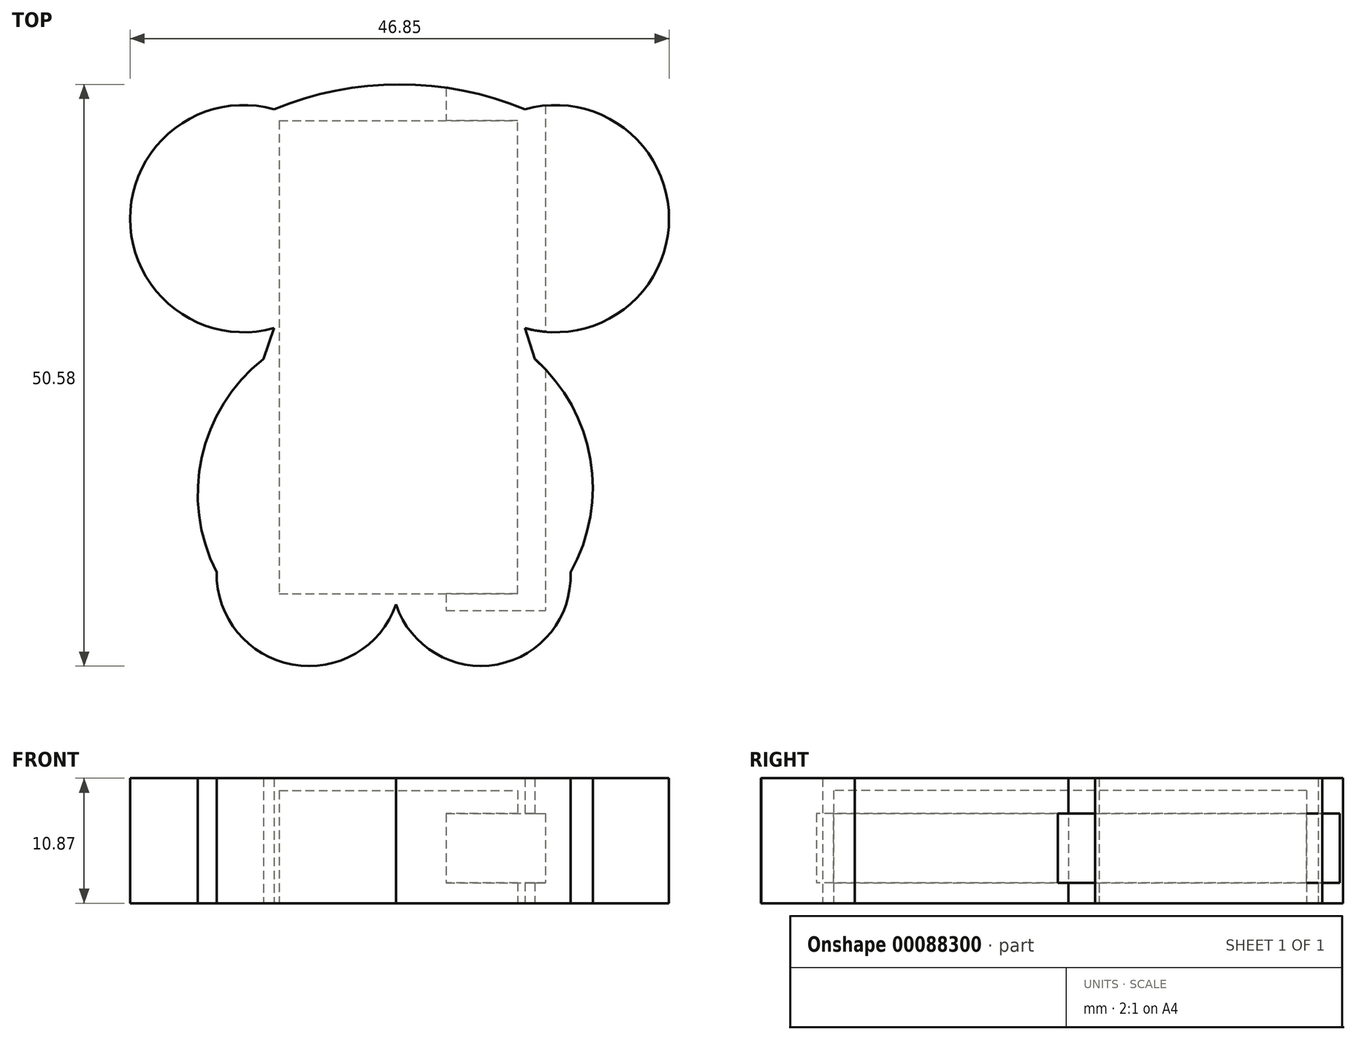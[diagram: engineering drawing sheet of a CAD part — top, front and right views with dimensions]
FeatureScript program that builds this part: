
annotation { "Feature Type Name" : "Feature", "Feature Type Description" : "" }
export const myFeature = defineFeature(function(context is Context, id is Id, definition is map)
    precondition{}
    {
        {
            var Q0;
            Q0=qCreatedBy(makeId("Top.planeOp"),FACE);
            var sketch = newSketch(context, id + "F0", { "sketchPlane" : qUnion([Q0])});
            skArc(sketch, "E0", {"start": v(-19.61, 43.61) * mm, "mid": v(-30.52, 45.76) * mm, "end": v(-41.42, 43.61) * mm});
            skArc(sketch, "E1", {"start": v(-19.61, 24.57) * mm, "mid": v(-7.1, 34.1) * mm, "end": v(-19.61, 43.61) * mm});
            skArc(sketch, "E2", {"start": v(-41.42, 43.61) * mm, "mid": v(-53.94, 34.1) * mm, "end": v(-41.42, 24.57) * mm});
            skLineSegment(sketch, "E3", {"start": v(-41.42, 24.57) * mm, "end": v(-42.36, 21.89) * mm});
            skLineSegment(sketch, "E4", {"start": v(-19.61, 24.57) * mm, "end": v(-18.76, 21.89) * mm});
            skArc(sketch, "E5", {"start": v(-42.36, 21.89) * mm, "mid": v(-47.71, 13.34) * mm, "end": v(-46.42, 3.33) * mm});
            skArc(sketch, "E6", {"start": v(-15.66, 3.33) * mm, "mid": v(-13.93, 13.16) * mm, "end": v(-18.76, 21.89) * mm});
            skArc(sketch, "E7", {"start": v(-30.75, 5.63) * mm, "mid": v(-24.6, -4.72) * mm, "end": v(-15.66, 3.33) * mm});
            skArc(sketch, "E8", {"start": v(-46.42, 3.33) * mm, "mid": v(-37.23, -4.74) * mm, "end": v(-30.75, 5.63) * mm});
            skSolve(sketch);
        }
        {
            var Q0;
            Q0 = qSketchRegion(id + "F0", true);
            extrude(context, id + "F1", {"entities" : qUnion([Q0]), "depth" : 10.87 * mm});
        }
        {
            var Q0;
            Q0=qCreatedBy(makeId("Top.planeOp"),FACE);
            var sketch = newSketch(context, id + "F2", { "sketchPlane" : qUnion([Q0])});
            skLineSegment(sketch, "E9.bottom", {"start": v(-40.99, 42.6) * mm, "end": v(-20.25, 42.6) * mm});
            skLineSegment(sketch, "E9.top", {"start": v(-40.99, 1.47) * mm, "end": v(-20.25, 1.47) * mm});
            skLineSegment(sketch, "E9.left", {"start": v(-40.99, 42.6) * mm, "end": v(-40.99, 1.47) * mm});
            skLineSegment(sketch, "E9.right", {"start": v(-20.25, 42.6) * mm, "end": v(-20.25, 1.47) * mm});
            skSolve(sketch);
        }
        {
            var Q0;
            Q0 = qSketchRegion(id + "F2", true);
            extrude(context, id + "F3", {"entities" : qUnion([Q0]), "operationType" : NewBodyOperationType.REMOVE, "depth" : 9.79 * mm});
        }
        {
            var Q0;
            Q0=qCreatedBy(makeId("Front.planeOp"),FACE);
            var sketch = newSketch(context, id + "F4", { "sketchPlane" : qUnion([Q0])});
            skLineSegment(sketch, "E10.bottom", {"start": v(-26.46, 7.78) * mm, "end": v(-17.83, 7.78) * mm});
            skLineSegment(sketch, "E10.top", {"start": v(-26.46, 1.78) * mm, "end": v(-17.83, 1.78) * mm});
            skLineSegment(sketch, "E10.left", {"start": v(-26.46, 7.78) * mm, "end": v(-26.46, 1.78) * mm});
            skLineSegment(sketch, "E10.right", {"start": v(-17.83, 7.78) * mm, "end": v(-17.83, 1.78) * mm});
            skSolve(sketch);
        }
        {
            var Q0;
            Q0 = qSketchRegion(id + "F4", true);
            extrude(context, id + "F5", {"entities" : qUnion([Q0]), "operationType" : NewBodyOperationType.REMOVE, "oppositeDirection" : true, "depth" : 63.14 * mm});
        }
    });
